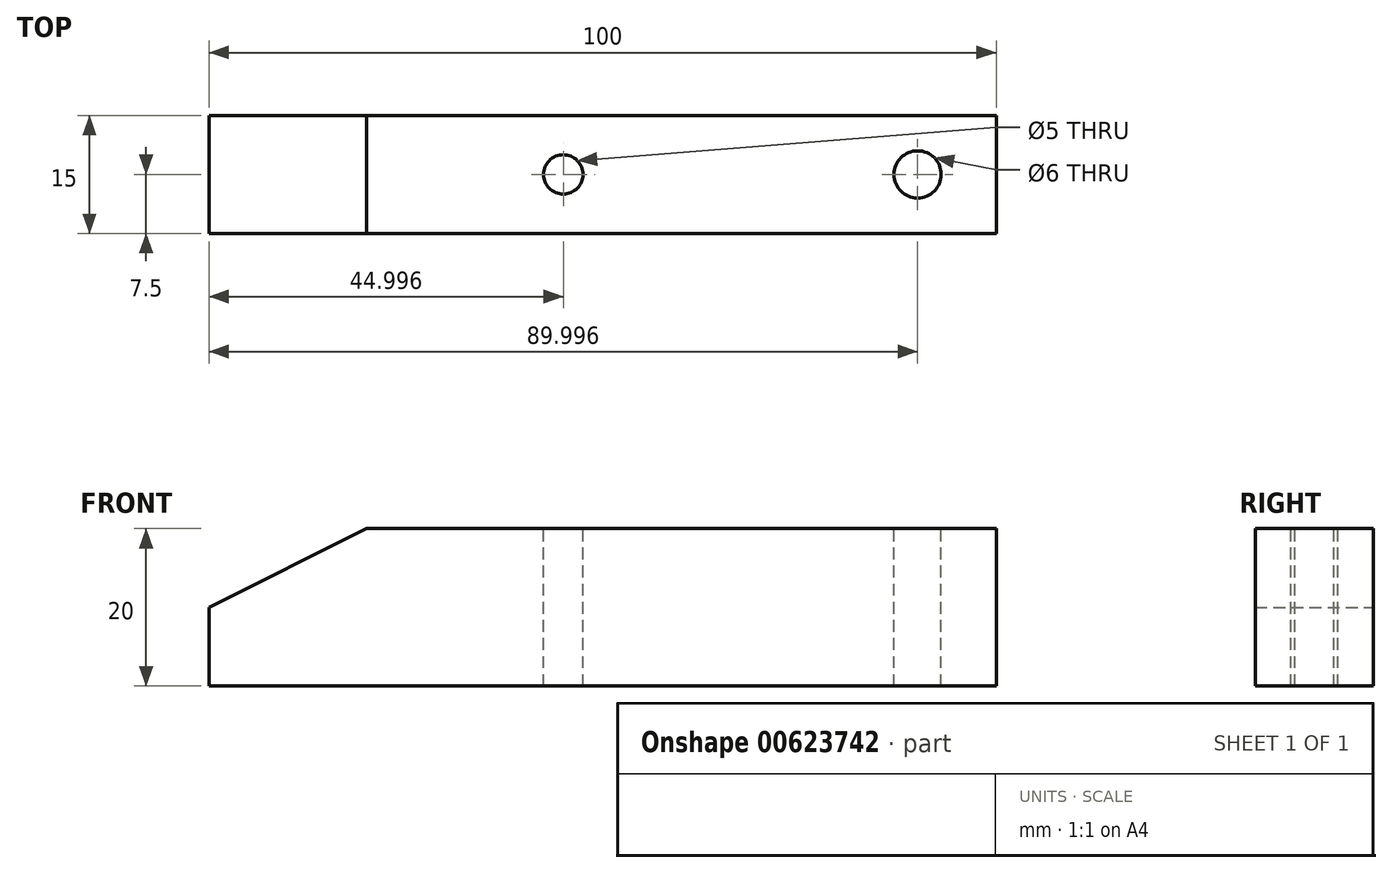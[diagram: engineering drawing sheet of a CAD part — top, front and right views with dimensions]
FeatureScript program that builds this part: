
annotation { "Feature Type Name" : "Feature", "Feature Type Description" : "" }
export const myFeature = defineFeature(function(context is Context, id is Id, definition is map)
    precondition{}
    {
        {
            var Q0;
            Q0=qCreatedBy(makeId("Front.planeOp"),FACE);
            var sketch = newSketch(context, id + "F0", { "sketchPlane" : qUnion([Q0])});
            skLineSegment(sketch, "E0", {"start": v(-43.11, 6.1) * mm, "end": v(56.89, 6.1) * mm});
            skLineSegment(sketch, "E1", {"start": v(56.89, 6.1) * mm, "end": v(56.89, 26.1) * mm});
            skLineSegment(sketch, "E2", {"start": v(-43.11, 6.1) * mm, "end": v(-43.11, 16.1) * mm});
            skLineSegment(sketch, "E3", {"start": v(56.89, 26.1) * mm, "end": v(-23.11, 26.1) * mm});
            skLineSegment(sketch, "E4", {"start": v(-43.11, 16.1) * mm, "end": v(-23.11, 26.1) * mm});
            skSolve(sketch);
        }
        {
            var Q0;
            Q0 = qSketchRegion(id + "F0", true);
            extrude(context, id + "F1", {"entities" : qUnion([Q0]), "depth" : 15 * mm, "offsetDistance" : 25 * mm});
        }
        {
            var Q0;
            Q0=makeQuery(id+"F1.opExtrude","SWEPT_FACE",FACE,{"disambiguationData":[OSD([sQuery(id+"F0.wireOp",EDGE,"E3")])]});
            var sketch = newSketch(context, id + "F2", { "sketchPlane" : qUnion([Q0])});
            skCircle(sketch, "E5", {"center": v(46.89, -7.5) * mm, "radius": 3 * mm});
            skLineSegment(sketch, "E6", {"start": v(1.89, -7.5) * mm, "end": v(1.89, -15) * mm, "construction": true});
            skLineSegment(sketch, "E7", {"start": v(-23.11, -7.5) * mm, "end": v(56.89, -7.5) * mm, "construction": true});
            skSolve(sketch);
        }
        {
            var Q0;
            Q0=sQuery(id+"F2.wireOp",VERTEX,"E6.start");
            var Q1;
            Q1=makeQuery(id+"F1.opExtrude","SWEPT_BODY",BODY,{"disambiguationData":[OSD([sQuery(id+"F0.wireOp",EDGE,"E0"),sQuery(id+"F0.wireOp",EDGE,"E1"),sQuery(id+"F0.wireOp",EDGE,"E2"),sQuery(id+"F0.wireOp",EDGE,"E3"),sQuery(id+"F0.wireOp",EDGE,"E4")])]});
            hole(context, id + "F3", {"style" : HoleStyle.SIMPLE, "endStyle" : HoleEndStyle.THROUGH, "standardTappedOrClearance" : lookupTablePath({ "standard" : "ISO", "engagement" : "75%", "pitch" : "1 mm", "size" : "M6", "type" : "Tapped" }), "standardBlindInLast" : lookupTablePath({ "standard" : "ISO", "engagement" : "75%", "pitch" : "1 mm", "size" : "M6", "type" : "Tapped" }), "holeDiameter" : 5 * mm, "majorDiameter" : 6 * mm, "showTappedDepth" : true, "isTappedThrough" : true, "tappedDepth" : 12 * mm, "tapClearance" : 3, "locations" : qUnion([Q0]), "scope" : qUnion([Q1])});
        }
        {
            var Q0;
            Q0 = qSketchRegion(id + "F2", true);
            extrude(context, id + "F4", {"entities" : qUnion([Q0]), "operationType" : NewBodyOperationType.REMOVE, "oppositeDirection" : true, "depth" : 25 * mm, "offsetDistance" : 25 * mm});
        }
    });
